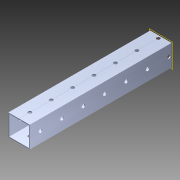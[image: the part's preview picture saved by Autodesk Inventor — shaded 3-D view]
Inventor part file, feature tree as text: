
AUTODESK INVENTOR PART (.ipt)
format: ipt  version: 2014 SP1 (Build 180222100, 222)  size: 1,146,368 bytes
history: native  units: in
note: dims shown in document units (in); Inventor stores cm internally (conversion verified against a paired STEP export)
features: pattern_circular x1, other x1, plane x1, extrude x1, imported_body x1, sketch x1
ambient origin geometry x8: Origin, YZ Plane, XZ Plane, XY Plane, X Axis, Y Axis, Z Axis, Center Point
bodies: Body1 (feature_tree)
feature tree (6):
  pattern_circular  "CirPattern2"
  other  "217-3426-STEP1"
  plane  "Work Plane1"
  extrude  "Extrusion1"  Depth=3937.0079in TaperAngle=0.0deg
  imported_body  "Base1"
  sketch  "Sketch1"  dims[d0=-6.625in d1=3937.0079in d2=0.0in]
